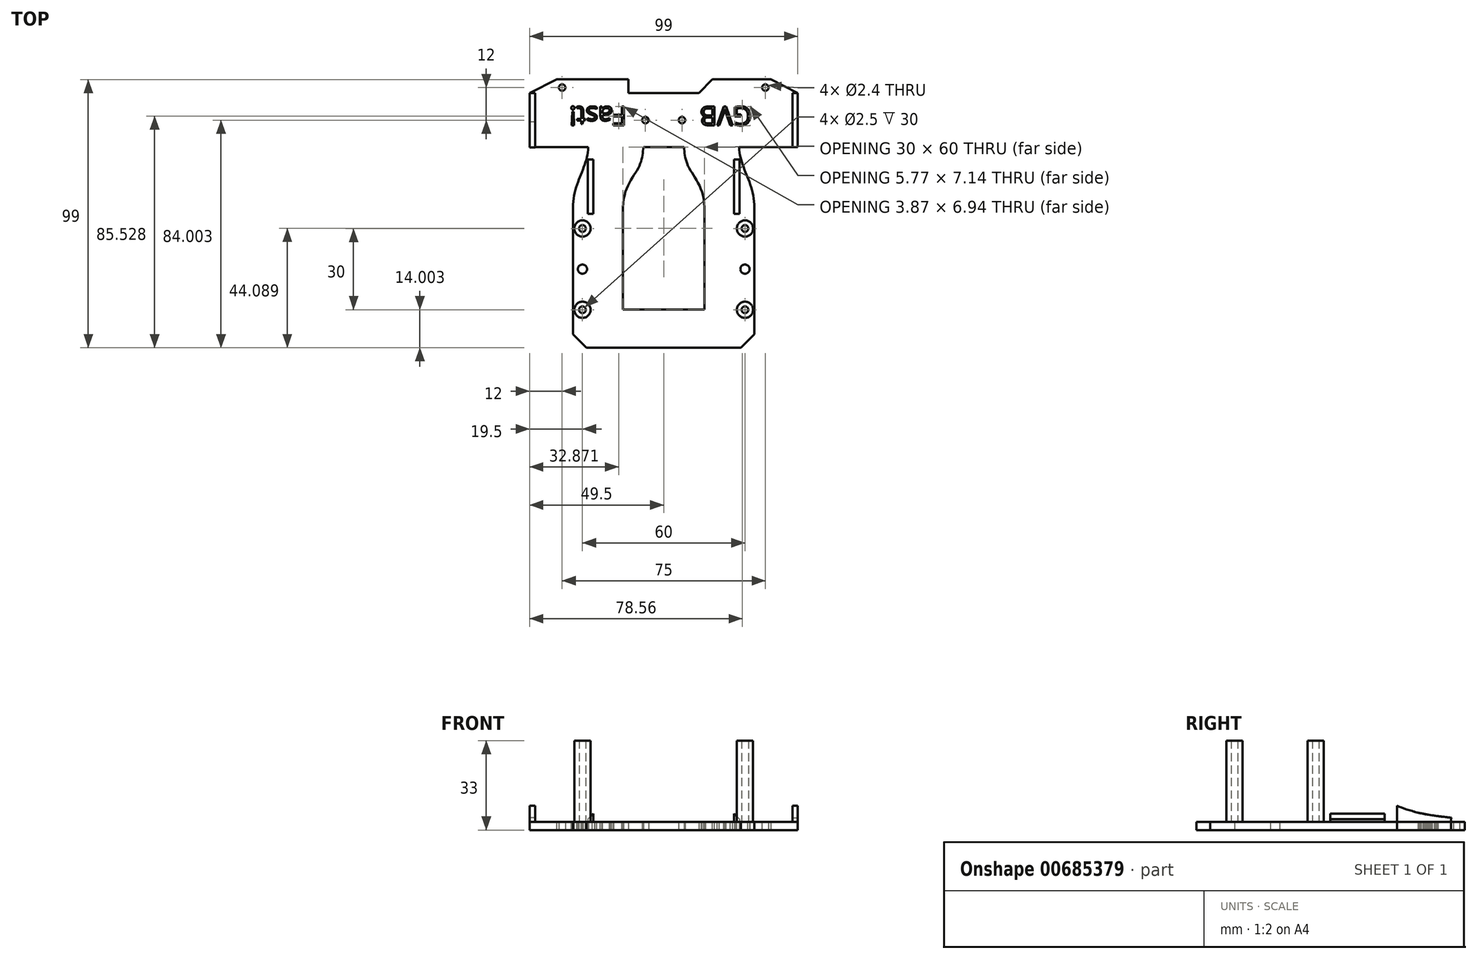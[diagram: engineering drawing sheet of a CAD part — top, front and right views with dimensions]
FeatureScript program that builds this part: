
annotation { "Feature Type Name" : "Feature", "Feature Type Description" : "" }
export const myFeature = defineFeature(function(context is Context, id is Id, definition is map)
    precondition{}
    {
        {
            var Q0;
            Q0=qCreatedBy(makeId("Top.planeOp"),FACE);
            var sketch = newSketch(context, id + "F0", { "sketchPlane" : qUnion([Q0])});
            skLineSegment(sketch, "E0", {"start": v(-49.5, 52.76) * mm, "end": v(-49.5, 27.76) * mm});
            skLineSegment(sketch, "E1", {"start": v(-49.5, 27.76) * mm, "end": v(-33.5, 27.76) * mm});
            skLineSegment(sketch, "E2", {"start": v(-33.5, 5.37) * mm, "end": v(-33.5, -46.24) * mm});
            skLineSegment(sketch, "E3", {"start": v(-33.5, -46.24) * mm, "end": v(0, -46.24) * mm});
            skLineSegment(sketch, "E4", {"start": v(-49.5, 52.76) * mm, "end": v(0, 52.76) * mm});
            skLineSegment(sketch, "E5.MirrorCS", {"start": v(49.5, 52.76) * mm, "end": v(0, 52.76) * mm});
            skLineSegment(sketch, "E6.MirrorCS", {"start": v(49.5, 52.76) * mm, "end": v(49.5, 27.76) * mm});
            skLineSegment(sketch, "E7.MirrorCS", {"start": v(49.5, 27.76) * mm, "end": v(33.5, 27.76) * mm});
            skLineSegment(sketch, "E8.MirrorCS", {"start": v(33.5, 5.37) * mm, "end": v(33.5, -46.24) * mm});
            skLineSegment(sketch, "E9.MirrorCS", {"start": v(33.5, -46.24) * mm, "end": v(0, -46.24) * mm});
            skCircle(sketch, "E10", {"center": v(-30, -17.24) * mm, "radius": 1.7 * mm});
            skCircle(sketch, "E11", {"center": v(-6.75, 37.76) * mm, "radius": 1.2 * mm});
            skCircle(sketch, "E12", {"center": v(-37.5, 49.76) * mm, "radius": 1.2 * mm});
            skCircle(sketch, "E13.MirrorC", {"center": v(6.75, 37.76) * mm, "radius": 1.2 * mm});
            skCircle(sketch, "E14.MirrorC", {"center": v(37.5, 49.76) * mm, "radius": 1.2 * mm});
            skCircle(sketch, "E15.MirrorC", {"center": v(30, -17.24) * mm, "radius": 1.7 * mm});
            skLineSegment(sketch, "E16", {"start": v(-33.5, 27.76) * mm, "end": v(-27.83, 27.76) * mm});
            skFitSpline(sketch, "E17", {"points": [v(-27.83, 27.76) * mm, v(-33.5, 5.37) * mm], "startDerivative": vector(-0.51, -22.67) * mm, "endDerivative": vector(0, -28.08) * mm});
            skFitSpline(sketch, "E18.MirrorCS", {"points": [v(27.83, 27.76) * mm, v(33.5, 5.37) * mm], "startDerivative": vector(0.51, -22.67) * mm, "endDerivative": vector(0, -28.08) * mm});
            skLineSegment(sketch, "E19.MirrorCS", {"start": v(33.5, 27.76) * mm, "end": v(27.83, 27.76) * mm});
            skPoint(sketch, "E20.orphan", {"position": v(33.5, 27.76) * mm});
            skSolve(sketch);
        }
        {
            var Q0;
            Q0=qSketchRegion(id+"F0",true);
            extrude(context, id + "F1", {"entities" : qUnion([Q0]), "depth" : 3 * mm, "offsetDistance" : 25 * mm});
        }
        {
            var Q0;
            Q0=makeQuery(id+"F1.opExtrude","CAP_FACE",FACE,{"disambiguationData":[OSD([sQuery(id+"F0.wireOp",EDGE,"E0"),sQuery(id+"F0.wireOp",EDGE,"E1"),sQuery(id+"F0.wireOp",EDGE,"E2"),sQuery(id+"F0.wireOp",EDGE,"E3"),sQuery(id+"F0.wireOp",EDGE,"E4"),sQuery(id+"F0.wireOp",EDGE,"E5.MirrorCS"),sQuery(id+"F0.wireOp",EDGE,"E6.MirrorCS"),sQuery(id+"F0.wireOp",EDGE,"E7.MirrorCS"),sQuery(id+"F0.wireOp",EDGE,"E8.MirrorCS"),sQuery(id+"F0.wireOp",EDGE,"E9.MirrorCS"),sQuery(id+"F0.wireOp",EDGE,"D2iVdyrN-lgH6-kqdr-8D6s-cuto2BwUotGw"),sQuery(id+"F0.wireOp",EDGE,"E10"),sQuery(id+"F0.wireOp",EDGE,"HQNJs8bB-sZYr-meKy-rgTR-hFvBVLR7mzoR"),sQuery(id+"F0.wireOp",EDGE,"wh96qxHu-Ra3m-NaDn-VShK-NLSfr9HxtLg7"),sQuery(id+"F0.wireOp",EDGE,"E11"),sQuery(id+"F0.wireOp",EDGE,"E12"),sQuery(id+"F0.wireOp",EDGE,"ClsNpT53-1d4u-9lEI-gExP-i9SNMVweOH6k"),sQuery(id+"F0.wireOp",EDGE,"E13.MirrorC"),sQuery(id+"F0.wireOp",EDGE,"02d239af-f542-472d-af80-28868edda1a60.MirrorC"),sQuery(id+"F0.wireOp",EDGE,"E14.MirrorC"),sQuery(id+"F0.wireOp",EDGE,"5721d74e-e26d-4e9d-980a-81192679cc150.MirrorC"),sQuery(id+"F0.wireOp",EDGE,"79b79993-8bfe-4dd2-98c9-0798df79eef40.MirrorC"),sQuery(id+"F0.wireOp",EDGE,"E15.MirrorC"),sQuery(id+"F0.wireOp",EDGE,"0fc6fcc7-77bf-4801-9c38-4061e79c6d3b0.MirrorC")])],"isStart":false});
            var sketch = newSketch(context, id + "F2", { "sketchPlane" : qUnion([Q0])});
            skSolve(sketch);
        }
        {
            var Q0;
            Q0=makeQuery(id+"F2.imprint","IMPRINT",FACE,{"disambiguationData":[TD([[makeQuery(id+"F2.imprint","IMPRINT",EDGE,{"derivedFrom":makeQuery(id+"F1.opExtrude","CAP_EDGE",EDGE,{"disambiguationData":[OSD([sQuery(id+"F0.wireOp",EDGE,"E0")])],"isStart":false})}),1.0]])]});
            var sketch = newSketch(context, id + "F3", { "sketchPlane" : qUnion([Q0])});
            skText(sketch, "E21", { "text": "GVB", "fontName": "OpenSans-Regular.ttf"});
            const initialGuessF3  = {"E21": [0.03254, 0.04276, -1, 0, 0.007]};
            skSetInitialGuess(sketch, initialGuessF3);
            skSolve(sketch);
        }
        {
            var Q0;
            Q0=qSketchRegion(id+"F3",true);
            var Q1;
            Q1=qSketchRegion(id+"F0",true);
            extrude(context, id + "F4", {"entities" : qUnion([Q0, Q1]), "operationType" : NewBodyOperationType.REMOVE, "oppositeDirection" : true, "depth" : 3 * mm, "offsetDistance" : 25 * mm});
        }
        {
            var Q0;
            Q0=makeQuery(id+"F2.imprint","IMPRINT",FACE,{"disambiguationData":[TD([[makeQuery(id+"F2.imprint","IMPRINT",EDGE,{"derivedFrom":makeQuery(id+"F1.opExtrude","CAP_EDGE",EDGE,{"disambiguationData":[OSD([sQuery(id+"F0.wireOp",EDGE,"E0")])],"isStart":false})}),1.0]])]});
            var sketch = newSketch(context, id + "F5", { "sketchPlane" : qUnion([Q0])});
            skText(sketch, "E22", { "text": "Fast!", "fontName": "OpenSans-Regular.ttf"});
            const initialGuessF5  = {"E22": [-0.01374, 0.04276, -1, 0, 0.007]};
            skSetInitialGuess(sketch, initialGuessF5);
            skSolve(sketch);
        }
        {
            var Q0;
            Q0 = qSketchRegion(id + "F5", true);
            extrude(context, id + "F6", {"entities" : qUnion([Q0]), "operationType" : NewBodyOperationType.REMOVE, "oppositeDirection" : true, "depth" : 3 * mm, "offsetDistance" : 25 * mm});
        }
        {
            var Q0;
            Q0=makeQuery(id+"F1.opExtrude","CAP_FACE",FACE,{"disambiguationData":[OSD([sQuery(id+"F0.wireOp",EDGE,"E0"),sQuery(id+"F0.wireOp",EDGE,"E1"),sQuery(id+"F0.wireOp",EDGE,"E2"),sQuery(id+"F0.wireOp",EDGE,"E3"),sQuery(id+"F0.wireOp",EDGE,"E4"),sQuery(id+"F0.wireOp",EDGE,"E5.MirrorCS"),sQuery(id+"F0.wireOp",EDGE,"E6.MirrorCS"),sQuery(id+"F0.wireOp",EDGE,"E7.MirrorCS"),sQuery(id+"F0.wireOp",EDGE,"E8.MirrorCS"),sQuery(id+"F0.wireOp",EDGE,"E9.MirrorCS"),sQuery(id+"F0.wireOp",EDGE,"D2iVdyrN-lgH6-kqdr-8D6s-cuto2BwUotGw"),sQuery(id+"F0.wireOp",EDGE,"E10"),sQuery(id+"F0.wireOp",EDGE,"HQNJs8bB-sZYr-meKy-rgTR-hFvBVLR7mzoR"),sQuery(id+"F0.wireOp",EDGE,"wh96qxHu-Ra3m-NaDn-VShK-NLSfr9HxtLg7"),sQuery(id+"F0.wireOp",EDGE,"E11"),sQuery(id+"F0.wireOp",EDGE,"E12"),sQuery(id+"F0.wireOp",EDGE,"ClsNpT53-1d4u-9lEI-gExP-i9SNMVweOH6k"),sQuery(id+"F0.wireOp",EDGE,"E13.MirrorC"),sQuery(id+"F0.wireOp",EDGE,"02d239af-f542-472d-af80-28868edda1a60.MirrorC"),sQuery(id+"F0.wireOp",EDGE,"E14.MirrorC"),sQuery(id+"F0.wireOp",EDGE,"5721d74e-e26d-4e9d-980a-81192679cc150.MirrorC"),sQuery(id+"F0.wireOp",EDGE,"79b79993-8bfe-4dd2-98c9-0798df79eef40.MirrorC"),sQuery(id+"F0.wireOp",EDGE,"E15.MirrorC"),sQuery(id+"F0.wireOp",EDGE,"0fc6fcc7-77bf-4801-9c38-4061e79c6d3b0.MirrorC")])],"isStart":true});
            var sketch = newSketch(context, id + "F7", { "sketchPlane" : qUnion([Q0])});
            skLineSegment(sketch, "E23.bottom", {"start": v(-13, -52.76) * mm, "end": v(0, -52.76) * mm});
            skLineSegment(sketch, "E23.top", {"start": v(-13, -47.76) * mm, "end": v(0, -47.76) * mm});
            skLineSegment(sketch, "E23.left", {"start": v(-13, -52.76) * mm, "end": v(-13, -47.76) * mm});
            skLineSegment(sketch, "E23.right", {"start": v(0, -52.76) * mm, "end": v(0, -47.76) * mm});
            skLineSegment(sketch, "E24.MirrorCS", {"start": v(13, -52.76) * mm, "end": v(13, -47.76) * mm});
            skLineSegment(sketch, "E25.MirrorCS", {"start": v(13, -47.76) * mm, "end": v(0, -47.76) * mm});
            skLineSegment(sketch, "E26.MirrorCS", {"start": v(13, -52.76) * mm, "end": v(0, -52.76) * mm});
            skLineSegment(sketch, "E27.bottom", {"start": v(-15, 32.15) * mm, "end": v(0, 32.15) * mm});
            skLineSegment(sketch, "E27.top", {"start": v(-7.5, -27.85) * mm, "end": v(0, -27.85) * mm});
            skLineSegment(sketch, "E27.left", {"start": v(-15, 32.15) * mm, "end": v(-15, -5.55) * mm});
            skLineSegment(sketch, "E27.right", {"start": v(0, 32.15) * mm, "end": v(0, -27.85) * mm});
            skLineSegment(sketch, "E28.MirrorCS", {"start": v(7.5, -27.85) * mm, "end": v(0, -27.85) * mm});
            skLineSegment(sketch, "E29.MirrorCS", {"start": v(15, 32.15) * mm, "end": v(15, -5.55) * mm});
            skLineSegment(sketch, "E30.MirrorCS", {"start": v(15, 32.15) * mm, "end": v(0, 32.15) * mm});
            skFitSpline(sketch, "E31", {"points": [v(-15, -5.55) * mm, v(-9.1, -20.63) * mm, v(-7.5, -27.85) * mm], "startDerivative": vector(-0.12, -37.27) * mm, "endDerivative": vector(1.39, -17.73) * mm});
            skFitSpline(sketch, "E32.MirrorCS", {"points": [v(15, -5.55) * mm, v(9.1, -20.63) * mm, v(7.5, -27.85) * mm], "startDerivative": vector(0.12, -37.27) * mm, "endDerivative": vector(-1.39, -17.73) * mm});
            skPoint(sketch, "E33.orphan", {"position": v(-15, -27.85) * mm});
            skPoint(sketch, "E34.orphan", {"position": v(15, -27.85) * mm});
            skSolve(sketch);
        }
        {
            var Q0;
            Q0 = qSketchRegion(id + "F7", true);
            extrude(context, id + "F8", {"entities" : qUnion([Q0]), "operationType" : NewBodyOperationType.REMOVE, "oppositeDirection" : true, "depth" : 3 * mm, "offsetDistance" : 25 * mm});
        }
        {
            var Q0;
            Q0=makeQuery(id+"F1.opExtrude","SWEPT_EDGE",EDGE,{"disambiguationData":[OSD([sQuery(id+"F0.wireOp",EDGE,"E5.MirrorCS"),sQuery(id+"F0.wireOp",EDGE,"E6.MirrorCS")])]});
            chamfer(context, id + "F9", {"entities" : qUnion([Q0]), "chamferType" : ChamferType.TWO_OFFSETS, "width1" : 10 * mm, "oppositeDirection" : false, "width2" : 5 * mm, "tangentPropagation" : true});
        }
        {
            var Q0;
            Q0=makeQuery(id+"F1.opExtrude","SWEPT_EDGE",EDGE,{"disambiguationData":[OSD([sQuery(id+"F0.wireOp",EDGE,"E0"),sQuery(id+"F0.wireOp",EDGE,"E4")])]});
            chamfer(context, id + "F10", {"entities" : qUnion([Q0]), "chamferType" : ChamferType.TWO_OFFSETS, "width1" : 5 * mm, "oppositeDirection" : false, "width2" : 10 * mm, "tangentPropagation" : true});
        }
        {
            var Q0;
            Q0=makeQuery(id+"F8.boolean.opBoolean","COPY",EDGE,{"derivedFrom":makeQuery(id+"F8.opExtrude","SWEPT_EDGE",EDGE,{"disambiguationData":[OSD([sQuery(id+"F0.wireOp",EDGE,"E4"),sQuery(id+"F0.wireOp",EDGE,"E5.MirrorCS"),sQuery(id+"F7.wireOp",EDGE,"E23.bottom"),sQuery(id+"F7.wireOp",EDGE,"E23.left")])]})});
            var Q1;
            Q1=makeQuery(id+"F8.boolean.opBoolean","COPY",EDGE,{"derivedFrom":makeQuery(id+"F8.opExtrude","SWEPT_EDGE",EDGE,{"disambiguationData":[OSD([sQuery(id+"F0.wireOp",EDGE,"E4"),sQuery(id+"F0.wireOp",EDGE,"E5.MirrorCS"),sQuery(id+"F7.wireOp",EDGE,"E24.MirrorCS"),sQuery(id+"F7.wireOp",EDGE,"E26.MirrorCS")])]})});
            var Q2;
            Q2=makeQuery(id+"F1.opExtrude","SWEPT_EDGE",EDGE,{"disambiguationData":[OSD([sQuery(id+"F0.wireOp",EDGE,"E8.MirrorCS"),sQuery(id+"F0.wireOp",EDGE,"E9.MirrorCS")])]});
            var Q3;
            Q3=makeQuery(id+"F1.opExtrude","SWEPT_EDGE",EDGE,{"disambiguationData":[OSD([sQuery(id+"F0.wireOp",EDGE,"E2"),sQuery(id+"F0.wireOp",EDGE,"E3")])]});
            chamfer(context, id + "F11", {"entities" : qUnion([Q0, Q1, Q2, Q3]), "width" : 5 * mm, "tangentPropagation" : true});
        }
        {
            var Q0;
            Q0=makeQuery(id+"F1.opExtrude","SWEPT_FACE",FACE,{"disambiguationData":[OSD([sQuery(id+"F0.wireOp",EDGE,"E6.MirrorCS")])]});
            var sketch = newSketch(context, id + "F12", { "sketchPlane" : qUnion([Q0])});
            skLineSegment(sketch, "E35", {"start": v(47.76, 3) * mm, "end": v(47.76, 4.5) * mm});
            skFitSpline(sketch, "E36", {"points": [v(47.76, 4.5) * mm, v(36.8, 6.1) * mm, v(24.88, 10.81) * mm, v(23.99, 12.55) * mm], "startDerivative": vector(-25.17, 3.08) * mm, "endDerivative": vector(-4.81, 7.19) * mm});
            skLineSegment(sketch, "E37", {"start": v(27.76, 3) * mm, "end": v(27.76, 9) * mm});
            skLineSegment(sketch, "E38", {"start": v(27.76, 3) * mm, "end": v(47.76, 3) * mm});
            skSolve(sketch);
        }
        {
            var Q0;
            Q0 = qSketchRegion(id + "F12", true);
            extrude(context, id + "F13", {"entities" : qUnion([Q0]), "oppositeDirection" : true, "depth" : 2 * mm, "offsetDistance" : 25 * mm});
        }
        {
            var Q0;
            Q0=makeQuery(id+"F1.opExtrude","SWEPT_FACE",FACE,{"disambiguationData":[OSD([sQuery(id+"F0.wireOp",EDGE,"E0")])]});
            var sketch = newSketch(context, id + "F14", { "sketchPlane" : qUnion([Q0])});
            skFitSpline(sketch, "E39.MirrorCS", {"points": [v(-47.8, 4.52) * mm, v(-36.65, 6.19) * mm, v(-24.85, 10.88) * mm, v(-24.18, 12.94) * mm], "startDerivative": vector(25.14, 3.3) * mm, "endDerivative": vector(4.84, 7.16) * mm});
            skLineSegment(sketch, "E40.MirrorCS", {"start": v(-27.73, 2.98) * mm, "end": v(-27.73, 8.98) * mm});
            skLineSegment(sketch, "E41.MirrorCS", {"start": v(-27.73, 2.98) * mm, "end": v(-47.73, 3.02) * mm});
            skLineSegment(sketch, "E42", {"start": v(-47.8, 4.52) * mm, "end": v(-47.73, 3.02) * mm});
            skSolve(sketch);
        }
        {
            var Q0;
            Q0 = qSketchRegion(id + "F14", true);
            extrude(context, id + "F15", {"entities" : qUnion([Q0]), "operationType" : NewBodyOperationType.ADD, "oppositeDirection" : true, "depth" : 2 * mm, "offsetDistance" : 25 * mm});
        }
        {
            var Q0;
            Q0=makeQuery(id+"F2.imprint","IMPRINT",FACE,{"disambiguationData":[TD([[makeQuery(id+"F2.imprint","IMPRINT",EDGE,{"derivedFrom":makeQuery(id+"F1.opExtrude","CAP_EDGE",EDGE,{"disambiguationData":[OSD([sQuery(id+"F0.wireOp",EDGE,"E0")])],"isStart":false})}),1.0]])]});
            var sketch = newSketch(context, id + "F16", { "sketchPlane" : qUnion([Q0])});
            skCircle(sketch, "E43", {"center": v(-30, -2.24) * mm, "radius": 3 * mm});
            skCircle(sketch, "E44", {"center": v(-30, -32.24) * mm, "radius": 3 * mm});
            skCircle(sketch, "E45", {"center": v(30, -2.24) * mm, "radius": 3 * mm});
            skCircle(sketch, "E46", {"center": v(30, -32.24) * mm, "radius": 3 * mm});
            skCircle(sketch, "E47", {"center": v(-30, -2.24) * mm, "radius": 1.25 * mm});
            skCircle(sketch, "E48", {"center": v(-30, -32.24) * mm, "radius": 1.25 * mm});
            skCircle(sketch, "E49", {"center": v(30, -2.24) * mm, "radius": 1.25 * mm});
            skCircle(sketch, "E50", {"center": v(30, -32.24) * mm, "radius": 1.25 * mm});
            skSolve(sketch);
        }
        {
            var Q0;
            Q0 = qSketchRegion(id + "F16", true);
            extrude(context, id + "F17", {"entities" : qUnion([Q0]), "operationType" : NewBodyOperationType.ADD, "depth" : 30 * mm, "offsetDistance" : 25 * mm});
        }
        {
            var Q0;
            Q0=makeQuery(id+"F2.imprint","IMPRINT",FACE,{"disambiguationData":[TD([[makeQuery(id+"F2.imprint","IMPRINT",EDGE,{"derivedFrom":makeQuery(id+"F1.opExtrude","CAP_EDGE",EDGE,{"disambiguationData":[OSD([sQuery(id+"F0.wireOp",EDGE,"E0")])],"isStart":false})}),1.0]])]});
            var sketch = newSketch(context, id + "F18", { "sketchPlane" : qUnion([Q0])});
            skLineSegment(sketch, "E51.bottom", {"start": v(-28, 23.17) * mm, "end": v(-26, 23.17) * mm});
            skLineSegment(sketch, "E51.top", {"start": v(-28, 3.17) * mm, "end": v(-26, 3.17) * mm});
            skLineSegment(sketch, "E51.left", {"start": v(-28, 23.17) * mm, "end": v(-28, 3.17) * mm});
            skLineSegment(sketch, "E51.right", {"start": v(-26, 23.17) * mm, "end": v(-26, 3.17) * mm});
            skLineSegment(sketch, "E52.MirrorCS", {"start": v(26, 23.17) * mm, "end": v(26, 3.17) * mm});
            skLineSegment(sketch, "E53.MirrorCS", {"start": v(28, 23.17) * mm, "end": v(28, 3.17) * mm});
            skLineSegment(sketch, "E54.MirrorCS", {"start": v(28, 23.17) * mm, "end": v(26, 23.17) * mm});
            skLineSegment(sketch, "E55.MirrorCS", {"start": v(28, 3.17) * mm, "end": v(26, 3.17) * mm});
            skSolve(sketch);
        }
        {
            var Q0;
            Q0 = qSketchRegion(id + "F18", true);
            extrude(context, id + "F19", {"entities" : qUnion([Q0]), "operationType" : NewBodyOperationType.ADD, "depth" : 3 * mm, "offsetDistance" : 25 * mm});
        }
        {
            var Q0;
            Q0=makeQuery(id+"F19.opExtrude","CAP_EDGE",EDGE,{"disambiguationData":[OSD([sQuery(id+"F18.wireOp",EDGE,"E51.left")])],"isStart":false});
            var Q1;
            Q1=makeQuery(id+"F19.opExtrude","CAP_EDGE",EDGE,{"disambiguationData":[OSD([sQuery(id+"F18.wireOp",EDGE,"E53.MirrorCS")])],"isStart":false});
            chamfer(context, id + "F20", {"entities" : qUnion([Q0, Q1]), "width" : 2 * mm, "tangentPropagation" : true});
        }
    });
